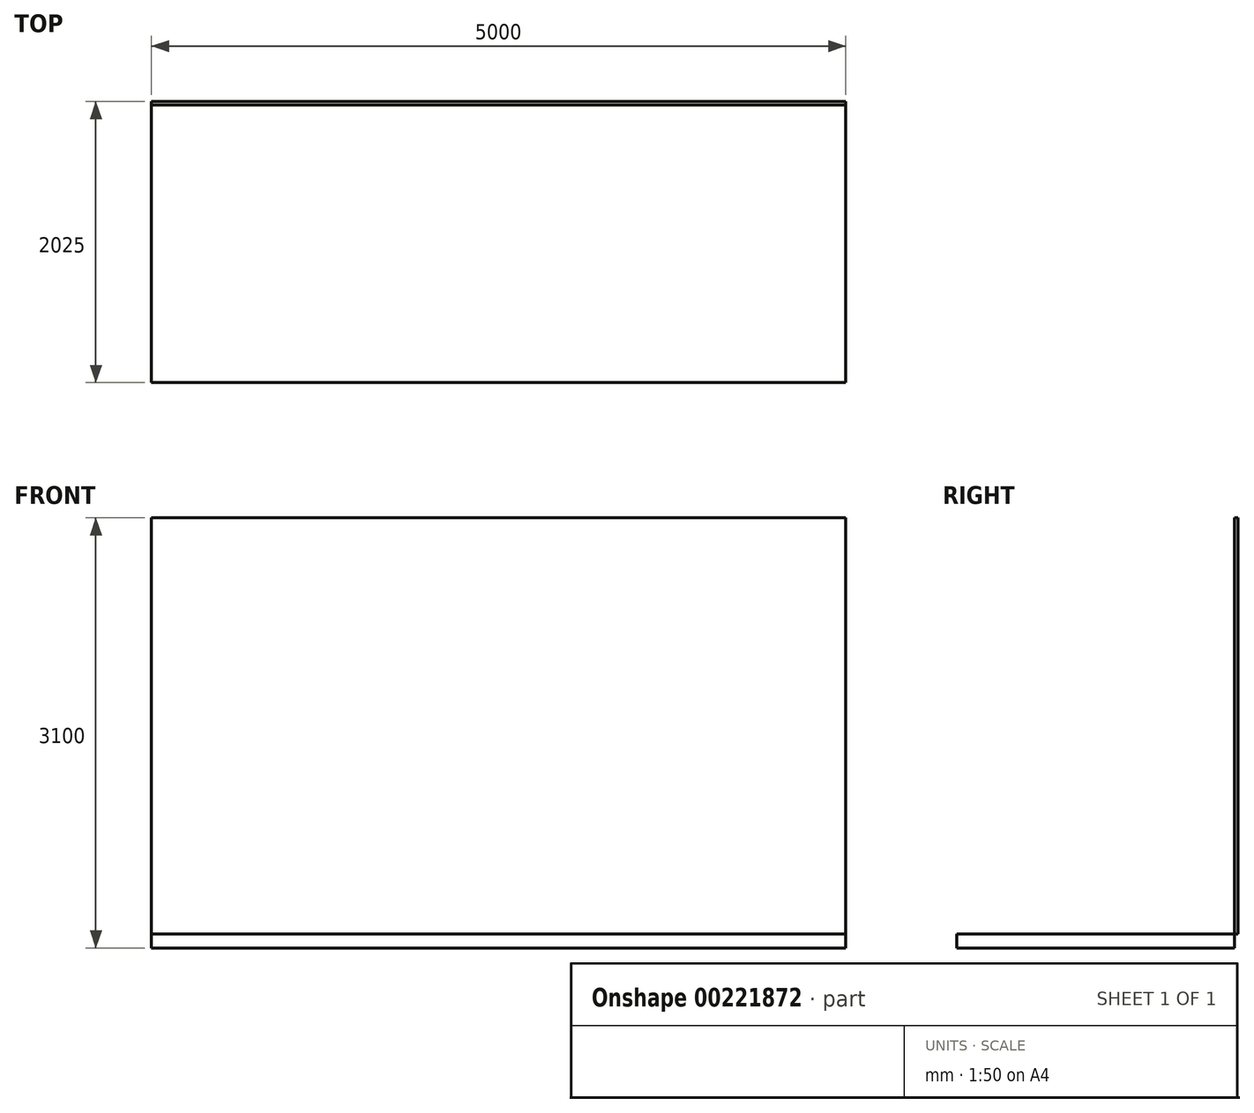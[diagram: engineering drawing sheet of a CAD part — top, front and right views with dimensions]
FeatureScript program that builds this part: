
annotation { "Feature Type Name" : "Feature", "Feature Type Description" : "" }
export const myFeature = defineFeature(function(context is Context, id is Id, definition is map)
    precondition{}
    {
        {
            var Q0;
            Q0=qCreatedBy(makeId("Top.planeOp"),FACE);
            var sketch = newSketch(context, id + "F0", { "sketchPlane" : qUnion([Q0])});
            skLineSegment(sketch, "E0.bottom", {"start": v(0, 0) * mm, "end": v(-5000, 0) * mm});
            skLineSegment(sketch, "E0.top", {"start": v(0, -2000) * mm, "end": v(-5000, -2000) * mm});
            skLineSegment(sketch, "E0.left", {"start": v(0, 0) * mm, "end": v(0, -2000) * mm});
            skLineSegment(sketch, "E0.right", {"start": v(-5000, 0) * mm, "end": v(-5000, -2000) * mm});
            skSolve(sketch);
        }
        {
            var Q0;
            Q0=makeQuery(id+"F0.imprint","IMPRINT",FACE,{"disambiguationData":[TD([[makeQuery(id+"F0.imprint","IMPRINT",EDGE,{"derivedFrom":sQuery(id+"F0.wireOp",EDGE,"E0.bottom")}),1.0]])]});
            extrude(context, id + "F1", {"entities" : qUnion([Q0]), "oppositeDirection" : true, "depth" : 100 * mm});
        }
        {
            var Q0;
            Q0=makeQuery(id+"F1.opExtrude","SWEPT_FACE",FACE,{"disambiguationData":[OSD([sQuery(id+"F0.wireOp",EDGE,"E0.bottom")])]});
            var sketch = newSketch(context, id + "F2", { "sketchPlane" : qUnion([Q0])});
            skLineSegment(sketch, "E1.bottom", {"start": v(5000, 0) * mm, "end": v(0, 0) * mm});
            skLineSegment(sketch, "E1.top", {"start": v(5000, 3000) * mm, "end": v(0, 3000) * mm});
            skLineSegment(sketch, "E1.left", {"start": v(5000, 0) * mm, "end": v(5000, 3000) * mm});
            skLineSegment(sketch, "E1.right", {"start": v(0, 0) * mm, "end": v(0, 3000) * mm});
            skSolve(sketch);
        }
        {
            var Q0;
            Q0=makeQuery(id+"F2.imprint","IMPRINT",FACE,{"disambiguationData":[TD([[makeQuery(id+"F2.imprint","IMPRINT",EDGE,{"derivedFrom":sQuery(id+"F2.wireOp",EDGE,"E1.bottom")}),1.0]])]});
            extrude(context, id + "F3", {"entities" : qUnion([Q0]), "depth" : 25 * mm});
        }
        {
            var Q0;
            Q0=makeQuery(id+"F1.opExtrude","SWEPT_FACE",FACE,{"disambiguationData":[OSD([sQuery(id+"F0.wireOp",EDGE,"E0.left")])]});
            cPlane(context, id + "F4", {"entities" : qUnion([Q0]), "cplaneType" : CPlaneType.OFFSET, "offset" : 2000 * mm, "oppositeDirection" : true, "width" : 150 * mm, "height" : 150 * mm});
        }
        {
            var Q0;
            Q0=qCreatedBy(id+"F4.planeOp",FACE);
            var sketch = newSketch(context, id + "F5", { "sketchPlane" : qUnion([Q0])});
            skLineSegment(sketch, "E2", {"start": v(-2005.4, 0) * mm, "end": v(-2005.4, 2000) * mm, "construction": true});
            skLineSegment(sketch, "E3", {"start": v(-2005.4, 2000) * mm, "end": v(0, 2500) * mm});
            skLineSegment(sketch, "E4", {"start": v(0, 2500) * mm, "end": v(0, 0) * mm, "construction": true});
            skLineSegment(sketch, "E5", {"start": v(-2005.4, 2000) * mm, "end": v(0, 2000) * mm, "construction": true});
            skSolve(sketch);
        }
        {
            var Q0;
            Q0 = qSketchRegion(id + "F5", true);
            var Q1;
            Q1=sQuery(id+"F5.wireOp",EDGE,"E3");
            extrude(context, id + "F6", {"entities" : qUnion([Q0]), "bodyType" : ToolBodyType.SURFACE, "surfaceEntities" : qUnion([Q1]), "endBound" : BoundingType.SYMMETRIC, "depth" : 7000 * mm});
        }
    });
